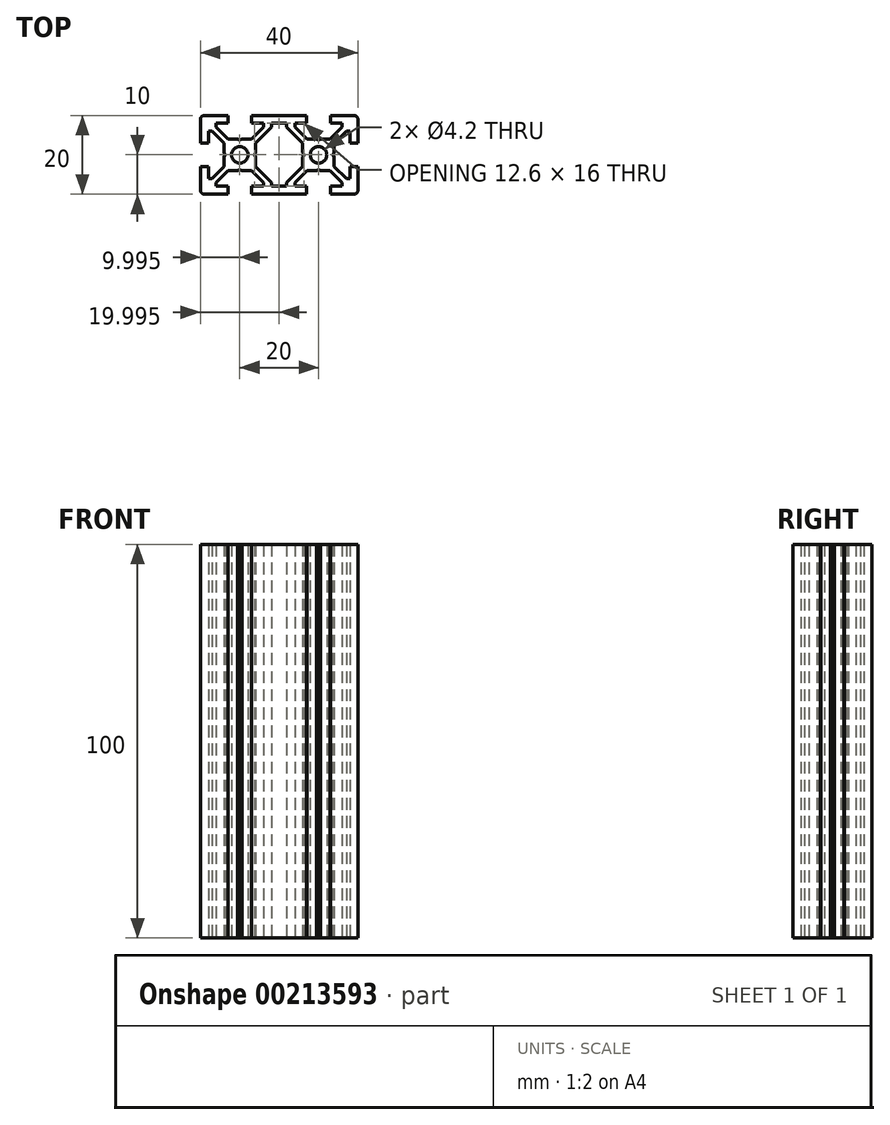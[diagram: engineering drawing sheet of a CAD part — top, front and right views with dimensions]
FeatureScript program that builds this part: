
annotation { "Feature Type Name" : "Feature", "Feature Type Description" : "" }
export const myFeature = defineFeature(function(context is Context, id is Id, definition is map)
    precondition{}
    {
        {
            var Q0;
            Q0=qCreatedBy(makeId("Top.planeOp"),FACE);
            var sketch = newSketch(context, id + "F0", { "sketchPlane" : qUnion([Q0])});
            skLineSegment(sketch, "E0.MirrorCS", {"start": v(6.14, -0.52) * mm, "end": v(6.44, 0) * mm});
            skLineSegment(sketch, "E1.MirrorCS", {"start": v(13.84, 0) * mm, "end": v(14.14, -0.52) * mm});
            skLineSegment(sketch, "E2.MirrorCS", {"start": v(10.65, -4) * mm, "end": v(10.14, -3.7) * mm});
            skLineSegment(sketch, "E3.MirrorCS", {"start": v(10.14, -3.7) * mm, "end": v(9.62, -4) * mm});
            skLineSegment(sketch, "E4.MirrorCS", {"start": v(4.14, -8) * mm, "end": v(7.14, -8) * mm});
            skLineSegment(sketch, "E5.MirrorCS", {"start": v(6.14, -2.94) * mm, "end": v(6.14, -0.52) * mm});
            skLineSegment(sketch, "E6.MirrorCS", {"start": v(16.14, -7.06) * mm, "end": v(13.07, -4) * mm});
            skLineSegment(sketch, "E7.MirrorCS", {"start": v(7.14, -8) * mm, "end": v(7.14, -10) * mm});
            skLineSegment(sketch, "E8.MirrorCS", {"start": v(20.14, -3) * mm, "end": v(20.14, -9) * mm});
            skLineSegment(sketch, "E9.MirrorCS", {"start": v(9.62, -4) * mm, "end": v(7.2, -4) * mm});
            skArc(sketch, "E10.MirrorCS", {"start": v(20.14, -9) * mm, "mid": v(19.84, -9.7) * mm, "end": v(19.14, -10) * mm});
            skLineSegment(sketch, "E11.MirrorCS", {"start": v(19.14, -10) * mm, "end": v(13.14, -10) * mm});
            skLineSegment(sketch, "E12.MirrorCS", {"start": v(13.07, -4) * mm, "end": v(10.65, -4) * mm});
            skLineSegment(sketch, "E13.MirrorCS", {"start": v(13.14, -10) * mm, "end": v(13.14, -8) * mm});
            skLineSegment(sketch, "E14.MirrorCS", {"start": v(14.14, -0.52) * mm, "end": v(14.14, -2.94) * mm});
            skLineSegment(sketch, "E15.MirrorCS", {"start": v(14.14, -2.94) * mm, "end": v(17.2, -6) * mm});
            skLineSegment(sketch, "E16.MirrorCS", {"start": v(17.2, -6) * mm, "end": v(18.14, -6) * mm});
            skLineSegment(sketch, "E17.MirrorCS", {"start": v(18.14, -6) * mm, "end": v(18.14, -3) * mm});
            skLineSegment(sketch, "E18.MirrorCS", {"start": v(18.14, -3) * mm, "end": v(20.14, -3) * mm});
            skLineSegment(sketch, "E19.MirrorCS", {"start": v(7.2, -4) * mm, "end": v(4.14, -7.06) * mm});
            skLineSegment(sketch, "E20.MirrorCS", {"start": v(13.14, -8) * mm, "end": v(16.14, -8) * mm});
            skLineSegment(sketch, "E21.MirrorCS", {"start": v(4.14, -7.06) * mm, "end": v(4.14, -8) * mm});
            skLineSegment(sketch, "E22.MirrorCS", {"start": v(16.14, -8) * mm, "end": v(16.14, -7.06) * mm});
            skLineSegment(sketch, "E23.MirrorCS", {"start": v(3.07, -6) * mm, "end": v(6.14, -2.94) * mm});
            skCircle(sketch, "E24", {"center": v(10.14, 0) * mm, "radius": 2.1 * mm});
            skLineSegment(sketch, "E25", {"start": v(3.07, -6) * mm, "end": v(2.01, -7.06) * mm});
            skLineSegment(sketch, "E26", {"start": v(2.01, -7.06) * mm, "end": v(2.01, -8) * mm});
            skLineSegment(sketch, "E27.MirrorCS", {"start": v(-10.38, -4) * mm, "end": v(-9.86, -3.7) * mm});
            skLineSegment(sketch, "E28.MirrorCS", {"start": v(-9.86, -3.7) * mm, "end": v(-9.35, -4) * mm});
            skLineSegment(sketch, "E29.MirrorCS", {"start": v(-13.56, 0) * mm, "end": v(-13.86, -0.52) * mm});
            skLineSegment(sketch, "E30.MirrorCS", {"start": v(-5.86, -0.52) * mm, "end": v(-6.16, 0) * mm});
            skLineSegment(sketch, "E31.MirrorCS", {"start": v(-12.86, -8) * mm, "end": v(-15.86, -8) * mm});
            skLineSegment(sketch, "E32.MirrorCS", {"start": v(-6.86, -8) * mm, "end": v(-6.86, -10) * mm});
            skLineSegment(sketch, "E33.MirrorCS", {"start": v(-19.86, -3) * mm, "end": v(-19.86, -9) * mm});
            skArc(sketch, "E34.MirrorCS", {"start": v(-19.86, -9) * mm, "mid": v(-19.57, -9.7) * mm, "end": v(-18.86, -10) * mm});
            skLineSegment(sketch, "E35.MirrorCS", {"start": v(-9.35, -4) * mm, "end": v(-6.93, -4) * mm});
            skLineSegment(sketch, "E36.MirrorCS", {"start": v(-18.86, -10) * mm, "end": v(-12.86, -10) * mm});
            skCircle(sketch, "E37.MirrorC", {"center": v(-9.86, 0) * mm, "radius": 2.1 * mm});
            skLineSegment(sketch, "E38.MirrorCS", {"start": v(-12.8, -4) * mm, "end": v(-10.38, -4) * mm});
            skLineSegment(sketch, "E39.MirrorCS", {"start": v(-17.86, -6) * mm, "end": v(-17.86, -3) * mm});
            skLineSegment(sketch, "E40.MirrorCS", {"start": v(-15.86, -8) * mm, "end": v(-15.86, -7.06) * mm});
            skLineSegment(sketch, "E41.MirrorCS", {"start": v(-13.86, -0.52) * mm, "end": v(-13.86, -2.94) * mm});
            skLineSegment(sketch, "E42.MirrorCS", {"start": v(-17.86, -3) * mm, "end": v(-19.86, -3) * mm});
            skLineSegment(sketch, "E43.MirrorCS", {"start": v(-13.86, -2.94) * mm, "end": v(-16.93, -6) * mm});
            skLineSegment(sketch, "E44.MirrorCS", {"start": v(-3.86, -8) * mm, "end": v(-6.86, -8) * mm});
            skLineSegment(sketch, "E45.MirrorCS", {"start": v(-15.86, -7.06) * mm, "end": v(-12.8, -4) * mm});
            skLineSegment(sketch, "E46.MirrorCS", {"start": v(-5.86, -2.94) * mm, "end": v(-5.86, -0.52) * mm});
            skLineSegment(sketch, "E47.MirrorCS", {"start": v(-6.93, -4) * mm, "end": v(-3.86, -7.06) * mm});
            skLineSegment(sketch, "E48.MirrorCS", {"start": v(-16.93, -6) * mm, "end": v(-17.86, -6) * mm});
            skLineSegment(sketch, "E49.MirrorCS", {"start": v(-1.74, -7.06) * mm, "end": v(-1.74, -8) * mm});
            skLineSegment(sketch, "E50.MirrorCS", {"start": v(-3.86, -7.06) * mm, "end": v(-3.86, -8) * mm});
            skLineSegment(sketch, "E51.MirrorCS", {"start": v(-2.8, -6) * mm, "end": v(-1.74, -7.06) * mm});
            skLineSegment(sketch, "E52.MirrorCS", {"start": v(-2.8, -6) * mm, "end": v(-5.86, -2.94) * mm});
            skLineSegment(sketch, "E53.MirrorCS", {"start": v(-12.86, -10) * mm, "end": v(-12.86, -8) * mm});
            skLineSegment(sketch, "E54.MirrorCS", {"start": v(10.14, 3.7) * mm, "end": v(9.62, 4) * mm});
            skLineSegment(sketch, "E55.MirrorCS", {"start": v(-10.38, 4) * mm, "end": v(-9.86, 3.7) * mm});
            skLineSegment(sketch, "E56.MirrorCS", {"start": v(10.65, 4) * mm, "end": v(10.14, 3.7) * mm});
            skLineSegment(sketch, "E57.MirrorCS", {"start": v(-9.86, 3.7) * mm, "end": v(-9.35, 4) * mm});
            skLineSegment(sketch, "E58.MirrorCS", {"start": v(13.84, 0) * mm, "end": v(14.14, 0.52) * mm});
            skLineSegment(sketch, "E59.MirrorCS", {"start": v(6.14, 0.52) * mm, "end": v(6.44, 0) * mm});
            skLineSegment(sketch, "E60.MirrorCS", {"start": v(-5.86, 0.52) * mm, "end": v(-6.16, 0) * mm});
            skLineSegment(sketch, "E61.MirrorCS", {"start": v(-13.56, 0) * mm, "end": v(-13.86, 0.52) * mm});
            skLineSegment(sketch, "E62.MirrorCS", {"start": v(-18.86, 10) * mm, "end": v(-12.86, 10) * mm});
            skLineSegment(sketch, "E63.MirrorCS", {"start": v(16.14, 7.06) * mm, "end": v(13.07, 4) * mm});
            skLineSegment(sketch, "E64.MirrorCS", {"start": v(6.14, 2.94) * mm, "end": v(6.14, 0.52) * mm});
            skLineSegment(sketch, "E65.MirrorCS", {"start": v(-3.86, 8) * mm, "end": v(-6.86, 8) * mm});
            skLineSegment(sketch, "E66.MirrorCS", {"start": v(4.14, 8) * mm, "end": v(7.14, 8) * mm});
            skLineSegment(sketch, "E67.MirrorCS", {"start": v(-15.86, 8) * mm, "end": v(-15.86, 7.06) * mm});
            skLineSegment(sketch, "E68.MirrorCS", {"start": v(-3.86, 7.06) * mm, "end": v(-3.86, 8) * mm});
            skArc(sketch, "E69.MirrorCS", {"start": v(20.14, 9) * mm, "mid": v(19.84, 9.7) * mm, "end": v(19.14, 10) * mm});
            skLineSegment(sketch, "E70.MirrorCS", {"start": v(14.14, 2.94) * mm, "end": v(17.2, 6) * mm});
            skLineSegment(sketch, "E71.MirrorCS", {"start": v(3.07, 6) * mm, "end": v(6.14, 2.94) * mm});
            skLineSegment(sketch, "E72.MirrorCS", {"start": v(-9.35, 4) * mm, "end": v(-6.93, 4) * mm});
            skLineSegment(sketch, "E73.MirrorCS", {"start": v(14.14, 0.52) * mm, "end": v(14.14, 2.94) * mm});
            skLineSegment(sketch, "E74.MirrorCS", {"start": v(-2.8, 6) * mm, "end": v(-5.86, 2.94) * mm});
            skLineSegment(sketch, "E75.MirrorCS", {"start": v(-17.86, 6) * mm, "end": v(-17.86, 3) * mm});
            skLineSegment(sketch, "E76.MirrorCS", {"start": v(16.14, 8) * mm, "end": v(16.14, 7.06) * mm});
            skLineSegment(sketch, "E77.MirrorCS", {"start": v(-15.86, 7.06) * mm, "end": v(-12.8, 4) * mm});
            skLineSegment(sketch, "E78.MirrorCS", {"start": v(18.14, 3) * mm, "end": v(20.14, 3) * mm});
            skLineSegment(sketch, "E79.MirrorCS", {"start": v(19.14, 10) * mm, "end": v(13.14, 10) * mm});
            skLineSegment(sketch, "E80.MirrorCS", {"start": v(4.14, 7.06) * mm, "end": v(4.14, 8) * mm});
            skLineSegment(sketch, "E81.MirrorCS", {"start": v(-12.86, 8) * mm, "end": v(-15.86, 8) * mm});
            skLineSegment(sketch, "E82.MirrorCS", {"start": v(-5.86, 2.94) * mm, "end": v(-5.86, 0.52) * mm});
            skLineSegment(sketch, "E83.MirrorCS", {"start": v(13.07, 4) * mm, "end": v(10.65, 4) * mm});
            skLineSegment(sketch, "E84.MirrorCS", {"start": v(-13.86, 2.94) * mm, "end": v(-16.93, 6) * mm});
            skLineSegment(sketch, "E85.MirrorCS", {"start": v(13.14, 8) * mm, "end": v(16.14, 8) * mm});
            skLineSegment(sketch, "E86.MirrorCS", {"start": v(-13.86, 0.52) * mm, "end": v(-13.86, 2.94) * mm});
            skLineSegment(sketch, "E87.MirrorCS", {"start": v(-6.86, 8) * mm, "end": v(-6.86, 10) * mm});
            skLineSegment(sketch, "E88.MirrorCS", {"start": v(20.14, 3) * mm, "end": v(20.14, 9) * mm});
            skLineSegment(sketch, "E89.MirrorCS", {"start": v(-12.8, 4) * mm, "end": v(-10.38, 4) * mm});
            skLineSegment(sketch, "E90.MirrorCS", {"start": v(-12.86, 10) * mm, "end": v(-12.86, 8) * mm});
            skLineSegment(sketch, "E91.MirrorCS", {"start": v(-6.93, 4) * mm, "end": v(-3.86, 7.06) * mm});
            skLineSegment(sketch, "E92.MirrorCS", {"start": v(9.62, 4) * mm, "end": v(7.2, 4) * mm});
            skLineSegment(sketch, "E93.MirrorCS", {"start": v(13.14, 10) * mm, "end": v(13.14, 8) * mm});
            skLineSegment(sketch, "E94.MirrorCS", {"start": v(-16.93, 6) * mm, "end": v(-17.86, 6) * mm});
            skLineSegment(sketch, "E95.MirrorCS", {"start": v(-19.86, 3) * mm, "end": v(-19.86, 9) * mm});
            skLineSegment(sketch, "E96.MirrorCS", {"start": v(3.07, 6) * mm, "end": v(2.01, 7.06) * mm});
            skLineSegment(sketch, "E97.MirrorCS", {"start": v(-17.86, 3) * mm, "end": v(-19.86, 3) * mm});
            skLineSegment(sketch, "E98.MirrorCS", {"start": v(-1.74, 7.06) * mm, "end": v(-1.74, 8) * mm});
            skLineSegment(sketch, "E99.MirrorCS", {"start": v(2.01, 7.06) * mm, "end": v(2.01, 8) * mm});
            skLineSegment(sketch, "E100.MirrorCS", {"start": v(18.14, 6) * mm, "end": v(18.14, 3) * mm});
            skArc(sketch, "E101.MirrorCS", {"start": v(-19.86, 9) * mm, "mid": v(-19.57, 9.7) * mm, "end": v(-18.86, 10) * mm});
            skLineSegment(sketch, "E102.MirrorCS", {"start": v(-2.8, 6) * mm, "end": v(-1.74, 7.06) * mm});
            skLineSegment(sketch, "E103.MirrorCS", {"start": v(7.14, 8) * mm, "end": v(7.14, 10) * mm});
            skLineSegment(sketch, "E104.MirrorCS", {"start": v(17.2, 6) * mm, "end": v(18.14, 6) * mm});
            skLineSegment(sketch, "E105.MirrorCS", {"start": v(7.2, 4) * mm, "end": v(4.14, 7.06) * mm});
            skLineSegment(sketch, "E106", {"start": v(7.14, -10) * mm, "end": v(-6.86, -10) * mm});
            skLineSegment(sketch, "E107", {"start": v(-1.74, -8) * mm, "end": v(2.01, -8) * mm});
            skLineSegment(sketch, "E108", {"start": v(-1.74, 8) * mm, "end": v(2.01, 8) * mm});
            skLineSegment(sketch, "E109", {"start": v(-6.86, 10) * mm, "end": v(7.14, 10) * mm});
            skLineSegment(sketch, "E110", {"start": v(-9.86, 0) * mm, "end": v(-19.86, 0) * mm, "construction": true});
            skSolve(sketch);
        }
        {
            var Q0;
            Q0=makeQuery(id+"F0.imprint","IMPRINT",FACE,{"disambiguationData":[TD([[makeQuery(id+"F0.imprint","IMPRINT",EDGE,{"derivedFrom":sQuery(id+"F0.wireOp",EDGE,"E0.MirrorCS")}),-1.0]])]});
            extrude(context, id + "F1", {"entities" : qUnion([Q0]), "depth" : 100 * mm});
        }
    });
